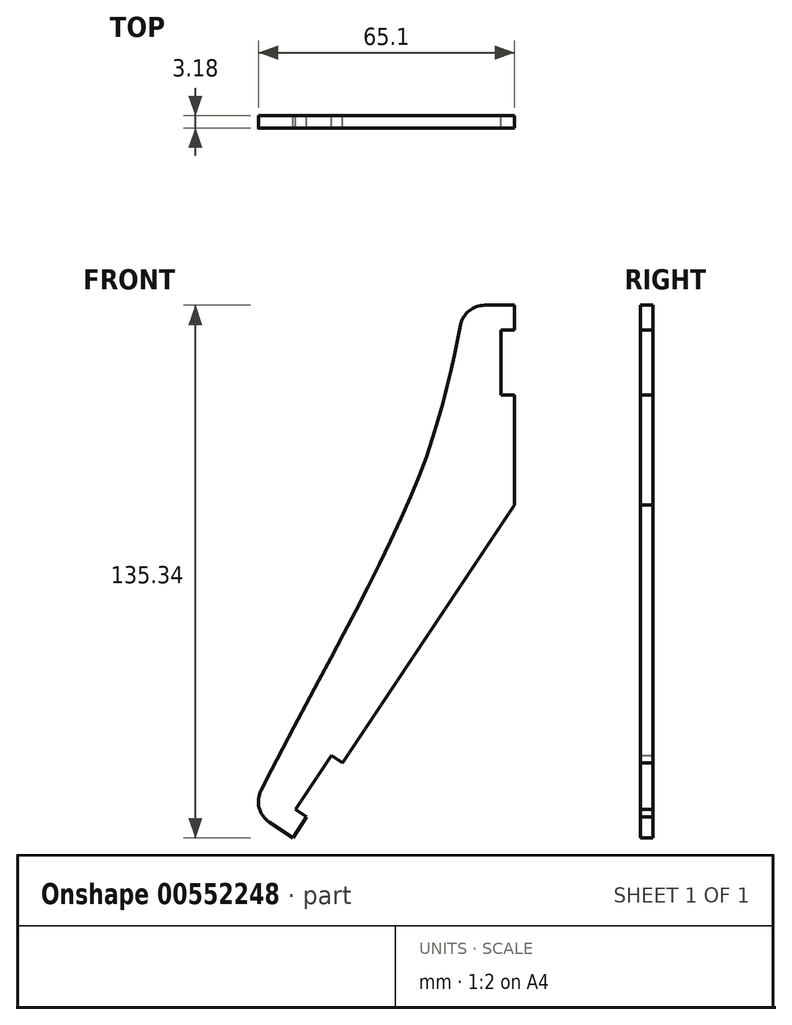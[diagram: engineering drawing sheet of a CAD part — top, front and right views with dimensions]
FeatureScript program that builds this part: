
annotation { "Feature Type Name" : "Feature", "Feature Type Description" : "" }
export const myFeature = defineFeature(function(context is Context, id is Id, definition is map)
    precondition{}
    {
        {
            var Q0;
            Q0=qCreatedBy(makeId("Front.planeOp"),FACE);
            var sketch = newSketch(context, id + "F0", { "sketchPlane" : qUnion([Q0])});
            skLineSegment(sketch, "E0", {"start": v(0, 50.8) * mm, "end": v(0, 44.45) * mm});
            skLineSegment(sketch, "E1", {"start": v(0, 27.94) * mm, "end": v(0, 0) * mm});
            skLineSegment(sketch, "E2", {"start": v(-56.36, -84.54) * mm, "end": v(-52.84, -79.25) * mm});
            skLineSegment(sketch, "E3", {"start": v(-43.68, -65.52) * mm, "end": v(0, 0) * mm});
            skLineSegment(sketch, "E4", {"start": v(0, 50.8) * mm, "end": v(-7.55, 50.8) * mm});
            skLineSegment(sketch, "E5", {"start": v(-56.36, -84.54) * mm, "end": v(-62.27, -80.6) * mm});
            skFitSpline(sketch, "E6", {"points": [v(-66.92, -77.5) * mm, v(-24.31, 7.36) * mm, v(-12.7, 50.8) * mm], "startDerivative": vector(58.45, 119.65) * mm, "endDerivative": vector(20.43, 93.72) * mm});
            skLineSegment(sketch, "E7", {"start": v(-3.43, 27.94) * mm, "end": v(-3.43, 44.45) * mm});
            skLineSegment(sketch, "E8", {"start": v(-3.43, 44.45) * mm, "end": v(0, 44.45) * mm});
            skLineSegment(sketch, "E9", {"start": v(-3.43, 27.94) * mm, "end": v(0, 27.94) * mm});
            skLineSegment(sketch, "E10", {"start": v(-55.69, -77.35) * mm, "end": v(-46.53, -63.61) * mm});
            skLineSegment(sketch, "E11", {"start": v(-46.53, -63.61) * mm, "end": v(-43.68, -65.52) * mm});
            skLineSegment(sketch, "E12", {"start": v(-55.69, -77.35) * mm, "end": v(-52.84, -79.25) * mm});
            skArc(sketch, "E13.filletArc", {"start": v(-7.55, 50.8) * mm, "mid": v(-11.56, 49.37) * mm, "end": v(-13.77, 45.72) * mm});
            skArc(sketch, "E14.filletArc", {"start": v(-64.41, -72.44) * mm, "mid": v(-64.89, -76.93) * mm, "end": v(-62.27, -80.6) * mm});
            skSolve(sketch);
        }
        {
            var Q0;
            Q0=makeQuery(id+"F0.imprint","IMPRINT",FACE,{"disambiguationData":[TD([[makeQuery(id+"F0.imprint","IMPRINT",EDGE,{"derivedFrom":sQuery(id+"F0.wireOp",EDGE,"E0")}),-1.0]])]});
            extrude(context, id + "F1", {"entities" : qUnion([Q0]), "depth" : 3.17 * mm, "offsetDistance" : 25.4 * mm});
        }
    });
